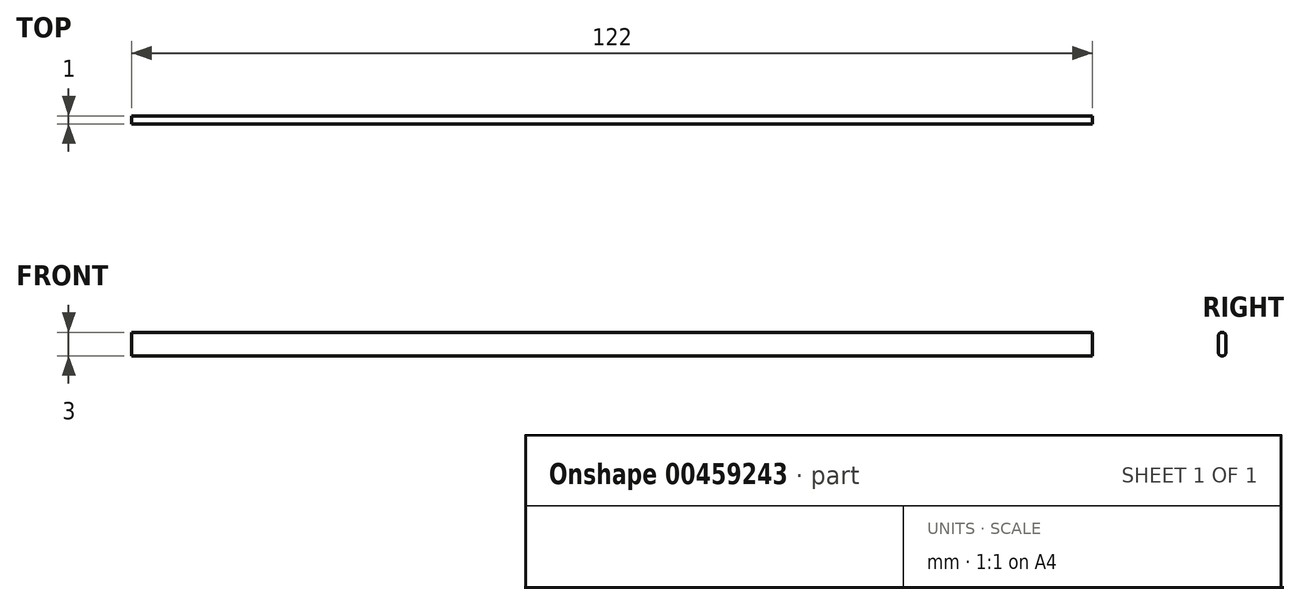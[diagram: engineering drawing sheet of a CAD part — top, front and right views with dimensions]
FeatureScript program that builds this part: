
annotation { "Feature Type Name" : "Feature", "Feature Type Description" : "" }
export const myFeature = defineFeature(function(context is Context, id is Id, definition is map)
    precondition{}
    {
        {
            var Q0;
            Q0=qCreatedBy(makeId("Right.planeOp"),FACE);
            var sketch = newSketch(context, id + "F0", { "sketchPlane" : qUnion([Q0])});
            skLineSegment(sketch, "E0.bottom", {"start": v(0.5, -1) * mm, "end": v(-0.5, -1) * mm, "construction": true});
            skLineSegment(sketch, "E0.top", {"start": v(0.5, 1) * mm, "end": v(-0.5, 1) * mm, "construction": true});
            skLineSegment(sketch, "E0.left", {"start": v(0.5, -1) * mm, "end": v(0.5, 1) * mm});
            skLineSegment(sketch, "E0.right", {"start": v(-0.5, -1) * mm, "end": v(-0.5, 1) * mm});
            skPoint(sketch, "E0.middle", {"position": v(0, 0) * mm});
            skArc(sketch, "E1", {"start": v(0.5, 1) * mm, "mid": v(0, 1.5) * mm, "end": v(-0.5, 1) * mm});
            skArc(sketch, "E2", {"start": v(-0.5, -1) * mm, "mid": v(0, -1.5) * mm, "end": v(0.5, -1) * mm});
            skSolve(sketch);
        }
        {
            var Q0;
            Q0 = qSketchRegion(id + "F0", true);
            extrude(context, id + "F1", {"entities" : qUnion([Q0]), "endBound" : BoundingType.SYMMETRIC, "depth" : 122 * mm});
        }
    });
